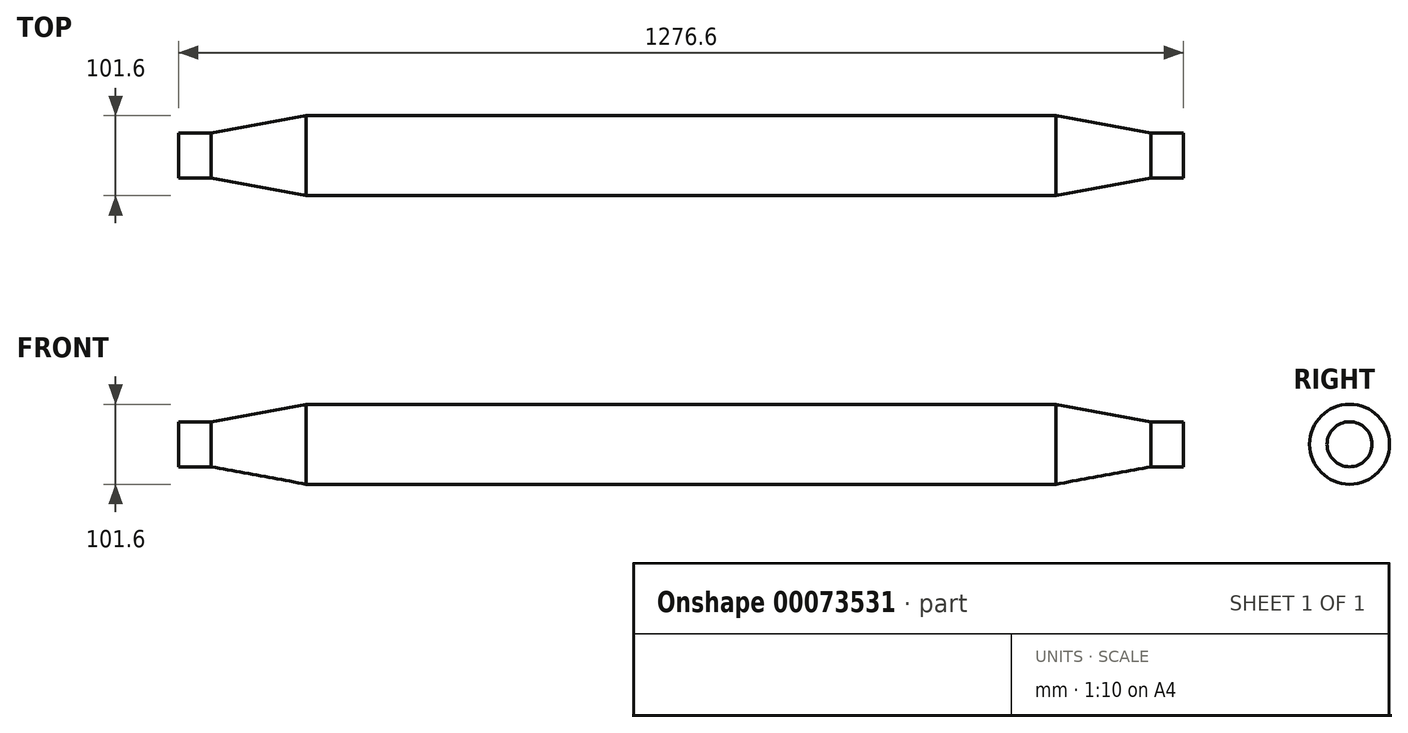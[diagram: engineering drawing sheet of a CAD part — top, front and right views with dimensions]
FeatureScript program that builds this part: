
annotation { "Feature Type Name" : "Feature", "Feature Type Description" : "" }
export const myFeature = defineFeature(function(context is Context, id is Id, definition is map)
    precondition{}
    {
        {
            var Q0;
            Q0=qCreatedBy(makeId("Right.planeOp"),FACE);
            var sketch = newSketch(context, id + "F0", { "sketchPlane" : qUnion([Q0])});
            skCircle(sketch, "E0", {"center": v(0, 0) * mm, "radius": 50.8 * mm});
            skSolve(sketch);
        }
        {
            var Q0;
            Q0 = qSketchRegion(id + "F0", true);
            extrude(context, id + "F1", {"entities" : qUnion([Q0]), "endBound" : BoundingType.SYMMETRIC, "depth" : 952.5 * mm});
        }
        {
            var Q0;
            Q0=qCreatedBy(makeId("Right.planeOp"),FACE);
            cPlane(context, id + "F2", {"entities" : qUnion([Q0]), "cplaneType" : CPlaneType.OFFSET, "offset" : 638.3 * mm, "width" : 152.4 * mm, "height" : 152.4 * mm});
        }
        {
            var Q0;
            Q0=qCreatedBy(id+"F2.planeOp",FACE);
            var sketch = newSketch(context, id + "F3", { "sketchPlane" : qUnion([Q0])});
            skCircle(sketch, "E1", {"center": v(0, 0) * mm, "radius": 28.58 * mm});
            skSolve(sketch);
        }
        {
            var Q0;
            Q0 = qSketchRegion(id + "F3", true);
            extrude(context, id + "F4", {"entities" : qUnion([Q0]), "oppositeDirection" : true, "depth" : 41.4 * mm});
        }
        {
            var Q0;
            Q0=makeQuery(id+"F4.opExtrude","SWEPT_BODY",BODY,{"disambiguationData":[OSD([sQuery(id+"F3.wireOp",EDGE,"E1")])]});
            var Q1;
            Q1=qCreatedBy(makeId("Right.planeOp"),FACE);
            mirror(context, id + "F5", {"entities" : qUnion([Q0]), "mirrorPlane" : qUnion([Q1])});
        }
        {
            var Q0;
            Q0=makeQuery(id+"F1.opExtrude","CAP_FACE",FACE,{"disambiguationData":[OSD([sQuery(id+"F0.wireOp",EDGE,"E0")])],"isStart":false});
            var Q1;
            Q1=makeQuery(id+"F4.opExtrude","CAP_FACE",FACE,{"disambiguationData":[OSD([sQuery(id+"F3.wireOp",EDGE,"E1")])],"isStart":false});
            loft(context, id + "F6", {"sheetProfilesArray" : [{ "sheetProfileEntities" : qUnion([Q0]) }, { "sheetProfileEntities" : qUnion([Q1]) }]});
        }
        {
            var Q0;
            Q0=makeQuery(id+"F1.opExtrude","CAP_FACE",FACE,{"disambiguationData":[OSD([sQuery(id+"F0.wireOp",EDGE,"E0")])],"isStart":true});
            var Q1;
            Q1=makeQuery(id+"F5.opPattern","COPY",FACE,{"derivedFrom":makeQuery(id+"F4.opExtrude","CAP_FACE",FACE,{"disambiguationData":[OSD([sQuery(id+"F3.wireOp",EDGE,"E1")])],"isStart":false}),"instanceName":"1"});
            loft(context, id + "F7", {"sheetProfilesArray" : [{ "sheetProfileEntities" : qUnion([Q0]) }, { "sheetProfileEntities" : qUnion([Q1]) }]});
        }
    });
